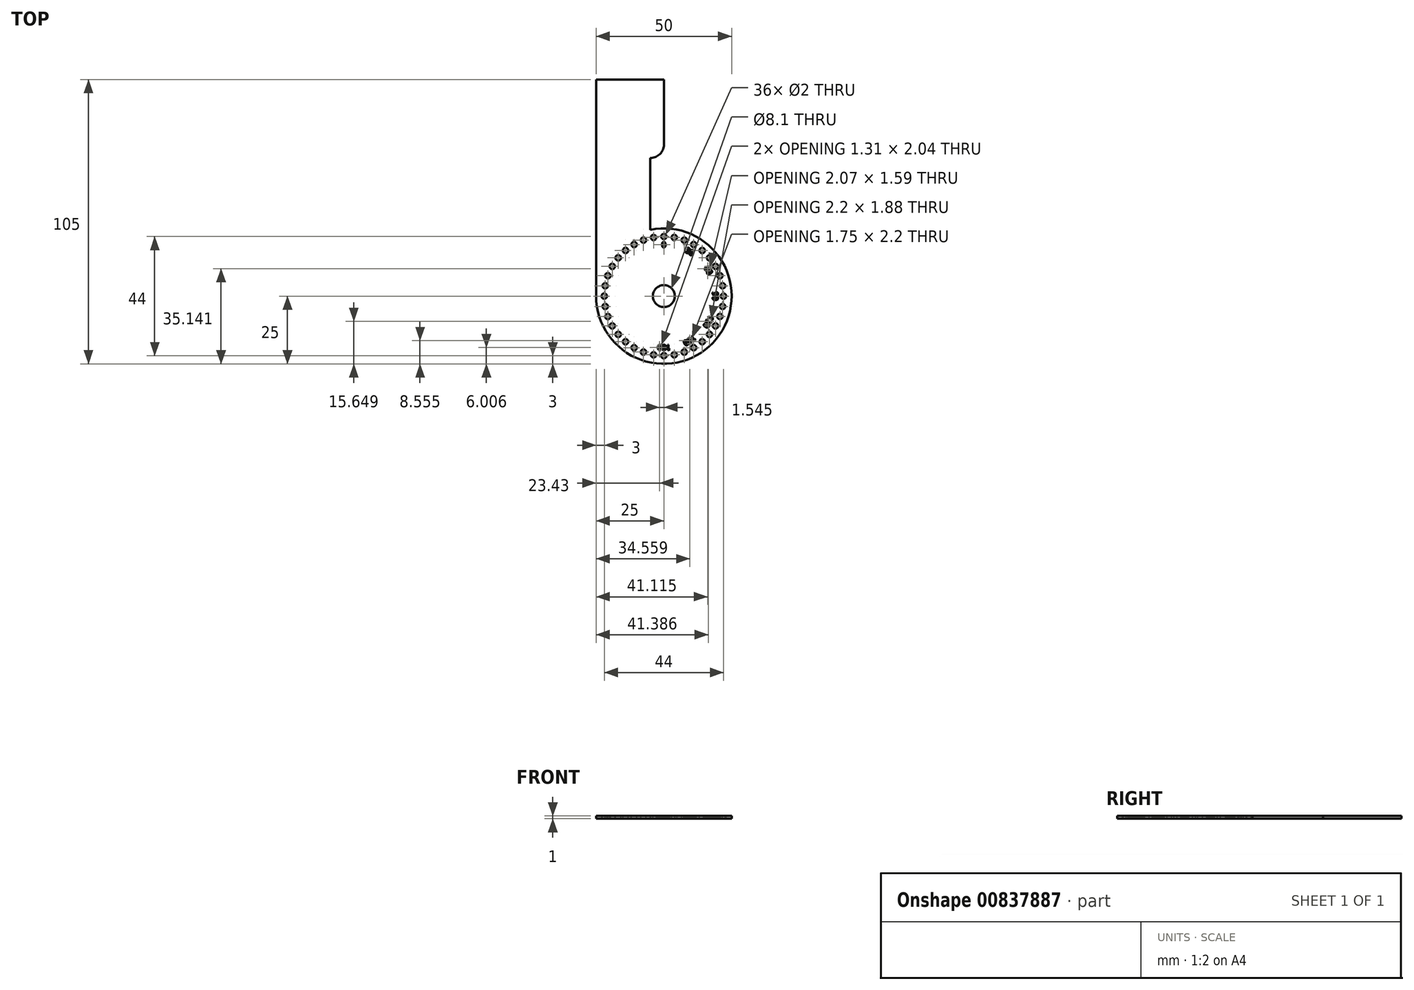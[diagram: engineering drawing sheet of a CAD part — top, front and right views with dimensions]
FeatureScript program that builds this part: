
annotation { "Feature Type Name" : "Feature", "Feature Type Description" : "" }
export const myFeature = defineFeature(function(context is Context, id is Id, definition is map)
    precondition{}
    {
        {
            var Q0;
            Q0=qCreatedBy(makeId("Top.planeOp"),FACE);
            var sketch = newSketch(context, id + "F0", { "sketchPlane" : qUnion([Q0])});
            skCircle(sketch, "E0", {"center": v(0, 0) * mm, "radius": 4.05 * mm});
            skCircle(sketch, "E1", {"center": v(0, 0) * mm, "radius": 25 * mm});
            skLineSegment(sketch, "E2.bottom", {"start": v(-25, 0) * mm, "end": v(25, 0) * mm});
            skLineSegment(sketch, "E2.top", {"start": v(-25, 80) * mm, "end": v(25, 80) * mm});
            skLineSegment(sketch, "E2.left", {"start": v(-25, 0) * mm, "end": v(-25, 80) * mm});
            skLineSegment(sketch, "E2.right", {"start": v(25, 0) * mm, "end": v(25, 80) * mm});
            skLineSegment(sketch, "E3.bottom", {"start": v(25, 65) * mm, "end": v(0, 65) * mm});
            skLineSegment(sketch, "E3.left", {"start": v(25, 65) * mm, "end": v(25, 35) * mm});
            skLineSegment(sketch, "E3.right", {"start": v(0, 65) * mm, "end": v(0, 60) * mm});
            skLineSegment(sketch, "E4", {"start": v(0, 60) * mm, "end": v(25, 35) * mm});
            skSolve(sketch);
        }
        {
            var Q0;
            {var subQ7=sQuery(id+"F0.wireOp",EDGE,"E2.top");Q0=makeQuery(id+"F0.imprint","IMPRINT",FACE,{"disambiguationData":[TD([[makeQuery(id+"F0.imprint","IMPRINT",EDGE,{"derivedFrom":subQ7}),-1.0]])]});}
            var Q1;
            {var subQ0=sQuery(id+"F0.wireOp",EDGE,"E2.bottom");var subQ1=sQuery(id+"F0.wireOp",EDGE,"E0");var subQ2=makeQuery(id+"F0.imprint","INTERSECT",VERTEX,{"disambiguationData":[OD(0.0)],"derivedFrom":[subQ1,subQ0]});Q1=makeQuery(id+"F0.imprint","IMPRINT",FACE,{"disambiguationData":[TD([[makeQuery(id+"F0.imprint","IMPRINT",EDGE,{"disambiguationData":[TD([[subQ2,1.0]])],"derivedFrom":subQ1}),-1.0]])]});}
            var Q2;
            {var subQ0=sQuery(id+"F0.wireOp",EDGE,"E2.bottom");var subQ1=sQuery(id+"F0.wireOp",EDGE,"E0");var subQ2=makeQuery(id+"F0.imprint","INTERSECT",VERTEX,{"disambiguationData":[OD(0.0)],"derivedFrom":[subQ1,subQ0]});Q2=makeQuery(id+"F0.imprint","IMPRINT",FACE,{"disambiguationData":[TD([[makeQuery(id+"F0.imprint","IMPRINT",EDGE,{"disambiguationData":[TD([[subQ2,-1.0]])],"derivedFrom":subQ1}),-1.0]])]});}
            var Q3;
            Q3=makeQuery(id+"F0.imprint","IMPRINT",FACE,{"disambiguationData":[TD([[makeQuery(id+"F0.imprint","IMPRINT",EDGE,{"derivedFrom":sQuery(id+"F0.wireOp",EDGE,"E3.bottom")}),1.0]])]});
            extrude(context, id + "F1", {"entities" : qUnion([Q0, Q1, Q2, Q3]), "oppositeDirection" : true, "depth" : 1 * mm, "offsetDistance" : 25 * mm});
        }
        {
            var Q0;
            Q0=makeQuery(id+"F1.opExtrude","CAP_FACE",FACE,{"disambiguationData":[OSD([sQuery(id+"F0.wireOp",EDGE,"E0"),sQuery(id+"F0.wireOp",EDGE,"E1"),sQuery(id+"F0.wireOp",EDGE,"E2.top"),sQuery(id+"F0.wireOp",EDGE,"E2.left"),sQuery(id+"F0.wireOp",EDGE,"E2.right"),sQuery(id+"F0.wireOp",EDGE,"E3.bottom"),sQuery(id+"F0.wireOp",EDGE,"E3.right"),sQuery(id+"F0.wireOp",EDGE,"E4")])],"isStart":true});
            var sketch = newSketch(context, id + "F2", { "sketchPlane" : qUnion([Q0])});
            skCircle(sketch, "E5", {"center": v(0, -22) * mm, "radius": 0.5 * mm});
            skPoint(sketch, "E5.centerSnap0", {"position": v(0, -25) * mm});
            skCircle(sketch, "E6.1.0", {"center": v(3.82, -21.67) * mm, "radius": 0.5 * mm});
            skCircle(sketch, "E6.2.0", {"center": v(7.52, -20.67) * mm, "radius": 0.5 * mm});
            skCircle(sketch, "E6.3.0", {"center": v(11, -19.05) * mm, "radius": 0.5 * mm});
            skCircle(sketch, "E6.4.0", {"center": v(14.14, -16.85) * mm, "radius": 0.5 * mm});
            skCircle(sketch, "E6.5.0", {"center": v(16.85, -14.14) * mm, "radius": 0.5 * mm});
            skCircle(sketch, "E6.6.0", {"center": v(19.05, -11) * mm, "radius": 0.5 * mm});
            skCircle(sketch, "E6.7.0", {"center": v(20.67, -7.52) * mm, "radius": 0.5 * mm});
            skCircle(sketch, "E6.8.0", {"center": v(21.67, -3.82) * mm, "radius": 0.5 * mm});
            skCircle(sketch, "E6.9.0", {"center": v(22, 0) * mm, "radius": 0.5 * mm});
            skCircle(sketch, "E6.10.0", {"center": v(21.67, 3.82) * mm, "radius": 0.5 * mm});
            skCircle(sketch, "E6.11.0", {"center": v(20.67, 7.52) * mm, "radius": 0.5 * mm});
            skCircle(sketch, "E6.12.0", {"center": v(19.05, 11) * mm, "radius": 0.5 * mm});
            skCircle(sketch, "E6.13.0", {"center": v(16.85, 14.14) * mm, "radius": 0.5 * mm});
            skCircle(sketch, "E6.14.0", {"center": v(14.14, 16.85) * mm, "radius": 0.5 * mm});
            skCircle(sketch, "E6.15.0", {"center": v(11, 19.05) * mm, "radius": 0.5 * mm});
            skCircle(sketch, "E6.16.0", {"center": v(7.52, 20.67) * mm, "radius": 0.5 * mm});
            skCircle(sketch, "E6.17.0", {"center": v(3.82, 21.67) * mm, "radius": 0.5 * mm});
            skCircle(sketch, "E6.18.0", {"center": v(0, 22) * mm, "radius": 0.5 * mm});
            skCircle(sketch, "E6.19.0", {"center": v(-3.82, 21.67) * mm, "radius": 0.5 * mm});
            skCircle(sketch, "E6.20.0", {"center": v(-7.52, 20.67) * mm, "radius": 0.5 * mm});
            skCircle(sketch, "E6.21.0", {"center": v(-11, 19.05) * mm, "radius": 0.5 * mm});
            skCircle(sketch, "E6.22.0", {"center": v(-14.14, 16.85) * mm, "radius": 0.5 * mm});
            skCircle(sketch, "E6.23.0", {"center": v(-16.85, 14.14) * mm, "radius": 0.5 * mm});
            skCircle(sketch, "E6.24.0", {"center": v(-19.05, 11) * mm, "radius": 0.5 * mm});
            skCircle(sketch, "E6.25.0", {"center": v(-20.67, 7.52) * mm, "radius": 0.5 * mm});
            skCircle(sketch, "E6.26.0", {"center": v(-21.67, 3.82) * mm, "radius": 0.5 * mm});
            skCircle(sketch, "E6.27.0", {"center": v(-22, 0) * mm, "radius": 0.5 * mm});
            skCircle(sketch, "E6.28.0", {"center": v(-21.67, -3.82) * mm, "radius": 0.5 * mm});
            skCircle(sketch, "E6.29.0", {"center": v(-20.67, -7.52) * mm, "radius": 0.5 * mm});
            skCircle(sketch, "E6.30.0", {"center": v(-19.05, -11) * mm, "radius": 0.5 * mm});
            skCircle(sketch, "E6.31.0", {"center": v(-16.85, -14.14) * mm, "radius": 0.5 * mm});
            skCircle(sketch, "E6.32.0", {"center": v(-14.14, -16.85) * mm, "radius": 0.5 * mm});
            skCircle(sketch, "E6.33.0", {"center": v(-11, -19.05) * mm, "radius": 0.5 * mm});
            skCircle(sketch, "E6.34.0", {"center": v(-7.52, -20.67) * mm, "radius": 0.5 * mm});
            skCircle(sketch, "E6.35.0", {"center": v(-3.82, -21.67) * mm, "radius": 0.5 * mm});
            skPoint(sketch, "E6.center", {"position": v(0, 0) * mm});
            skSolve(sketch);
        }
        {
            var Q0;
            Q0=sQuery(id+"F2.wireOp",VERTEX,"E5.center");
            var Q1;
            Q1=sQuery(id+"F2.wireOp",VERTEX,"E6.center");
            var Q2;
            Q2=sQuery(id+"F2.wireOp",VERTEX,"E6.61.0.center");
            var Q3;
            Q3=sQuery(id+"F2.wireOp",VERTEX,"E6.2.0.center");
            var Q4;
            Q4=sQuery(id+"F2.wireOp",VERTEX,"E6.49.0.center");
            var Q5;
            Q5=sQuery(id+"F2.wireOp",VERTEX,"E6.38.0.center");
            var Q6;
            Q6=sQuery(id+"F2.wireOp",VERTEX,"E6.1.0.center");
            var Q7;
            Q7=sQuery(id+"F2.wireOp",VERTEX,"E6.27.0.center");
            var Q8;
            Q8=sQuery(id+"F2.wireOp",VERTEX,"E6.8.0.center");
            var Q9;
            Q9=sQuery(id+"F2.wireOp",VERTEX,"E6.63.0.center");
            var Q10;
            Q10=sQuery(id+"F2.wireOp",VERTEX,"E6.28.0.center");
            var Q11;
            Q11=sQuery(id+"F2.wireOp",VERTEX,"E6.62.0.center");
            var Q12;
            Q12=sQuery(id+"F2.wireOp",VERTEX,"E6.66.0.center");
            var Q13;
            Q13=sQuery(id+"F2.wireOp",VERTEX,"E6.6.0.center");
            var Q14;
            Q14=sQuery(id+"F2.wireOp",VERTEX,"E6.58.0.center");
            var Q15;
            Q15=sQuery(id+"F2.wireOp",VERTEX,"E6.23.0.center");
            var Q16;
            Q16=sQuery(id+"F2.wireOp",VERTEX,"E6.26.0.center");
            var Q17;
            Q17=sQuery(id+"F2.wireOp",VERTEX,"E6.53.0.center");
            var Q18;
            Q18=sQuery(id+"F2.wireOp",VERTEX,"E6.13.0.center");
            var Q19;
            Q19=sQuery(id+"F2.wireOp",VERTEX,"E6.71.0.center");
            var Q20;
            Q20=sQuery(id+"F2.wireOp",VERTEX,"E6.34.0.center");
            var Q21;
            Q21=sQuery(id+"F2.wireOp",VERTEX,"E6.20.0.center");
            var Q22;
            Q22=sQuery(id+"F2.wireOp",VERTEX,"E6.59.0.center");
            var Q23;
            Q23=sQuery(id+"F2.wireOp",VERTEX,"E6.54.0.center");
            var Q24;
            Q24=sQuery(id+"F2.wireOp",VERTEX,"E6.22.0.center");
            var Q25;
            Q25=sQuery(id+"F2.wireOp",VERTEX,"E6.9.0.center");
            var Q26;
            Q26=sQuery(id+"F2.wireOp",VERTEX,"E6.32.0.center");
            var Q27;
            Q27=sQuery(id+"F2.wireOp",VERTEX,"E6.25.0.center");
            var Q28;
            Q28=sQuery(id+"F2.wireOp",VERTEX,"E6.64.0.center");
            var Q29;
            Q29=sQuery(id+"F2.wireOp",VERTEX,"E6.47.0.center");
            var Q30;
            Q30=sQuery(id+"F2.wireOp",VERTEX,"E6.31.0.center");
            var Q31;
            Q31=sQuery(id+"F2.wireOp",VERTEX,"E6.4.0.center");
            var Q32;
            Q32=sQuery(id+"F2.wireOp",VERTEX,"E6.15.0.center");
            var Q33;
            Q33=sQuery(id+"F2.wireOp",VERTEX,"E6.24.0.center");
            var Q34;
            Q34=sQuery(id+"F2.wireOp",VERTEX,"E6.29.0.center");
            var Q35;
            Q35=sQuery(id+"F2.wireOp",VERTEX,"E6.52.0.center");
            var Q36;
            Q36=sQuery(id+"F2.wireOp",VERTEX,"E6.7.0.center");
            var Q37;
            Q37=sQuery(id+"F2.wireOp",VERTEX,"E6.45.0.center");
            var Q38;
            Q38=sQuery(id+"F2.wireOp",VERTEX,"E6.42.0.center");
            var Q39;
            Q39=sQuery(id+"F2.wireOp",VERTEX,"E6.36.0.center");
            var Q40;
            Q40=sQuery(id+"F2.wireOp",VERTEX,"E6.17.0.center");
            var Q41;
            Q41=sQuery(id+"F2.wireOp",VERTEX,"E6.68.0.center");
            var Q42;
            Q42=sQuery(id+"F2.wireOp",VERTEX,"E6.18.0.center");
            var Q43;
            Q43=sQuery(id+"F2.wireOp",VERTEX,"E6.69.0.center");
            var Q44;
            Q44=sQuery(id+"F2.wireOp",VERTEX,"E6.56.0.center");
            var Q45;
            Q45=sQuery(id+"F2.wireOp",VERTEX,"E6.70.0.center");
            var Q46;
            Q46=sQuery(id+"F2.wireOp",VERTEX,"E6.48.0.center");
            var Q47;
            Q47=sQuery(id+"F2.wireOp",VERTEX,"E6.33.0.center");
            var Q48;
            Q48=sQuery(id+"F2.wireOp",VERTEX,"E6.10.0.center");
            var Q49;
            Q49=sQuery(id+"F2.wireOp",VERTEX,"E6.39.0.center");
            var Q50;
            Q50=sQuery(id+"F2.wireOp",VERTEX,"E6.55.0.center");
            var Q51;
            Q51=sQuery(id+"F2.wireOp",VERTEX,"E6.14.0.center");
            var Q52;
            Q52=sQuery(id+"F2.wireOp",VERTEX,"E6.21.0.center");
            var Q53;
            Q53=sQuery(id+"F2.wireOp",VERTEX,"E6.16.0.center");
            var Q54;
            Q54=sQuery(id+"F2.wireOp",VERTEX,"E6.65.0.center");
            var Q55;
            Q55=sQuery(id+"F2.wireOp",VERTEX,"E6.41.0.center");
            var Q56;
            Q56=sQuery(id+"F2.wireOp",VERTEX,"E6.3.0.center");
            var Q57;
            Q57=sQuery(id+"F2.wireOp",VERTEX,"E6.67.0.center");
            var Q58;
            Q58=sQuery(id+"F2.wireOp",VERTEX,"E6.19.0.center");
            var Q59;
            Q59=sQuery(id+"F2.wireOp",VERTEX,"E6.11.0.center");
            var Q60;
            Q60=sQuery(id+"F2.wireOp",VERTEX,"E6.57.0.center");
            var Q61;
            Q61=sQuery(id+"F2.wireOp",VERTEX,"E6.37.0.center");
            var Q62;
            Q62=sQuery(id+"F2.wireOp",VERTEX,"E6.51.0.center");
            var Q63;
            Q63=sQuery(id+"F2.wireOp",VERTEX,"E6.12.0.center");
            var Q64;
            Q64=sQuery(id+"F2.wireOp",VERTEX,"E6.50.0.center");
            var Q65;
            Q65=sQuery(id+"F2.wireOp",VERTEX,"E6.44.0.center");
            var Q66;
            Q66=sQuery(id+"F2.wireOp",VERTEX,"E6.35.0.center");
            var Q67;
            Q67=sQuery(id+"F2.wireOp",VERTEX,"E6.60.0.center");
            var Q68;
            Q68=sQuery(id+"F2.wireOp",VERTEX,"E6.5.0.center");
            var Q69;
            Q69=sQuery(id+"F2.wireOp",VERTEX,"E6.46.0.center");
            var Q70;
            Q70=sQuery(id+"F2.wireOp",VERTEX,"E6.43.0.center");
            var Q71;
            Q71=sQuery(id+"F2.wireOp",VERTEX,"E6.30.0.center");
            var Q72;
            Q72=sQuery(id+"F2.wireOp",VERTEX,"E6.40.0.center");
            var Q73;
            Q73=makeQuery(id+"F1.opExtrude","SWEPT_BODY",BODY,{"disambiguationData":[OSD([sQuery(id+"F0.wireOp",EDGE,"E0"),sQuery(id+"F0.wireOp",EDGE,"E1"),sQuery(id+"F0.wireOp",EDGE,"E2.top"),sQuery(id+"F0.wireOp",EDGE,"E2.left"),sQuery(id+"F0.wireOp",EDGE,"E2.right"),sQuery(id+"F0.wireOp",EDGE,"E3.bottom"),sQuery(id+"F0.wireOp",EDGE,"E3.right"),sQuery(id+"F0.wireOp",EDGE,"E4")])]});
            hole(context, id + "F3", {"style" : HoleStyle.SIMPLE, "endStyle" : HoleEndStyle.THROUGH, "holeDiameter" : 2 * mm, "majorDiameter" : 5 * mm, "isTappedThrough" : true, "tappedDepth" : 12 * mm, "tapClearance" : 3, "locations" : qUnion([Q0, Q1, Q2, Q3, Q4, Q5, Q6, Q7, Q8, Q9, Q10, Q11, Q12, Q13, Q14, Q15, Q16, Q17, Q18, Q19, Q20, Q21, Q22, Q23, Q24, Q25, Q26, Q27, Q28, Q29, Q30, Q31, Q32, Q33, Q34, Q35, Q36, Q37, Q38, Q39, Q40, Q41, Q42, Q43, Q44, Q45, Q46, Q47, Q48, Q49, Q50, Q51, Q52, Q53, Q54, Q55, Q56, Q57, Q58, Q59, Q60, Q61, Q62, Q63, Q64, Q65, Q66, Q67, Q68, Q69, Q70, Q71, Q72]), "scope" : qUnion([Q73])});
        }
        {
            var Q0;
            Q0=makeQuery(id+"F1.opExtrude","CAP_FACE",FACE,{"disambiguationData":[OSD([sQuery(id+"F0.wireOp",EDGE,"E0"),sQuery(id+"F0.wireOp",EDGE,"E1"),sQuery(id+"F0.wireOp",EDGE,"E2.top"),sQuery(id+"F0.wireOp",EDGE,"E2.left"),sQuery(id+"F0.wireOp",EDGE,"E2.right"),sQuery(id+"F0.wireOp",EDGE,"E3.bottom"),sQuery(id+"F0.wireOp",EDGE,"E3.right"),sQuery(id+"F0.wireOp",EDGE,"E4")])],"isStart":true});
            var sketch = newSketch(context, id + "F4", { "sketchPlane" : qUnion([Q0])});
            skText(sketch, "E7", { "text": "0", "fontName": "OpenSans-Regular.ttf"});
            const initialGuessF4  = {"E7": [-0.00082, 0.018, 1, 0, 0.002]};
            skSetInitialGuess(sketch, initialGuessF4);
            skSolve(sketch);
        }
        {
            var Q0;
            Q0 = qSketchRegion(id + "F4", true);
            extrude(context, id + "F5", {"entities" : qUnion([Q0]), "operationType" : NewBodyOperationType.REMOVE, "endBound" : BoundingType.UP_TO_NEXT, "oppositeDirection" : true, "depth" : 25 * mm, "offsetDistance" : 25 * mm});
        }
        {
            var Q0;
            {var subQ0=sQuery(id+"F0.wireOp",EDGE,"E2.left");var subQ1=sQuery(id+"F0.wireOp",EDGE,"E4");var subQ2=sQuery(id+"F0.wireOp",EDGE,"E0");var subQ3=sQuery(id+"F0.wireOp",EDGE,"E3.right");var subQ4=sQuery(id+"F0.wireOp",EDGE,"E2.right");var subQ5=sQuery(id+"F0.wireOp",EDGE,"E2.top");var subQ6=sQuery(id+"F0.wireOp",EDGE,"E1");var subQ7=sQuery(id+"F0.wireOp",EDGE,"E3.bottom");Q0=makeQuery(id+"F5.boolean.opBoolean","SPLIT",FACE,{"disambiguationData":[TD([makeQuery(id+"F1.opExtrude","SWEPT_FACE",FACE,{"disambiguationData":[OSD([subQ2])]})])],"derivedFrom":makeQuery(id+"F1.opExtrude","CAP_FACE",FACE,{"disambiguationData":[OSD([subQ2,subQ6,subQ5,subQ0,subQ4,subQ7,subQ3,subQ1])],"isStart":true})});}
            var sketch = newSketch(context, id + "F6", { "sketchPlane" : qUnion([Q0])});
            skText(sketch, "E8", { "text": "30\n", "fontName": "OpenSans-Regular.ttf"});
            skText(sketch, "E9", { "text": "90", "fontName": "OpenSans-Regular.ttf"});
            skLineSegment(sketch, "E10", {"start": v(0, 0) * mm, "end": v(9, 15.59) * mm, "construction": true});
            skLineSegment(sketch, "E11", {"start": v(0, 0) * mm, "end": v(4.05, 0) * mm, "construction": true});
            skText(sketch, "E12", { "text": "60", "fontName": "OpenSans-Regular.ttf"});
            skLineSegment(sketch, "E13", {"start": v(0, 0) * mm, "end": v(15.59, 9) * mm, "construction": true});
            skPoint(sketch, "E14.center", {"position": v(0, 0) * mm});
            const initialGuessF6  = {"E8": [0.0076, 0.0164, 0.86603, -0.5, 0.002], "E9": [0.018, 0.0016, 0, -1, 0.002], "E12": [0.01478, 0.0104, 0.5, -0.86603, 0.002]};
            skSetInitialGuess(sketch, initialGuessF6);
            skSolve(sketch);
        }
        {
            var Q0;
            Q0 = qSketchRegion(id + "F6", true);
            extrude(context, id + "F7", {"entities" : qUnion([Q0]), "operationType" : NewBodyOperationType.REMOVE, "oppositeDirection" : true, "depth" : 25 * mm, "offsetDistance" : 25 * mm});
        }
        {
            var Q0;
            {var subQ3=sQuery(id+"F0.wireOp",EDGE,"E4");var subQ5=sQuery(id+"F0.wireOp",EDGE,"E2.right");var subQ6=sQuery(id+"F0.wireOp",EDGE,"E2.top");var subQ8=sQuery(id+"F0.wireOp",EDGE,"E3.right");var subQ11=sQuery(id+"F0.wireOp",EDGE,"E2.left");var subQ13=sQuery(id+"F0.wireOp",EDGE,"E1");var subQ15=sQuery(id+"F0.wireOp",EDGE,"E0");var subQ16=makeQuery(id+"F1.opExtrude","SWEPT_FACE",FACE,{"disambiguationData":[OSD([subQ15])]});var subQ35=sQuery(id+"F0.wireOp",EDGE,"E3.bottom");Q0=makeQuery(id+"F7.boolean.opBoolean","SPLIT",FACE,{"disambiguationData":[TD([subQ16])],"derivedFrom":makeQuery(id+"F5.boolean.opBoolean","SPLIT",FACE,{"disambiguationData":[TD([subQ16])],"derivedFrom":makeQuery(id+"F1.opExtrude","CAP_FACE",FACE,{"disambiguationData":[OSD([subQ15,subQ13,subQ6,subQ11,subQ5,subQ35,subQ8,subQ3])],"isStart":true})})});}
            var sketch = newSketch(context, id + "F8", { "sketchPlane" : qUnion([Q0])});
            skLineSegment(sketch, "E15", {"start": v(0, 0) * mm, "end": v(4.05, 0) * mm, "construction": true});
            skLineSegment(sketch, "E16", {"start": v(0, 0) * mm, "end": v(15.59, -9) * mm, "construction": true});
            skLineSegment(sketch, "E17", {"start": v(0, 0) * mm, "end": v(9, -15.59) * mm, "construction": true});
            skLineSegment(sketch, "E18", {"start": v(0, 0) * mm, "end": v(0, -18) * mm, "construction": true});
            skText(sketch, "E19", { "text": "150", "fontName": "OpenSans-Regular.ttf"});
            skText(sketch, "E20", { "text": "180", "fontName": "OpenSans-Regular.ttf"});
            skText(sketch, "E21", { "text": "120", "fontName": "OpenSans-Regular.ttf"});
            skText(sketch, "E22", { "text": "120", "fontName": "OpenSans-Regular.ttf"});
            const initialGuessF8  = {"E19": [0.01108, -0.01439, -0.86603, -0.5, 0.002], "E20": [0.0024, -0.018, -1, 0, 0.002], "E21": [0.0168, -0.00692, -0.5, -0.86603, 0.002], "E22": [0.1751, 0.04347, 1, 0, 0.002]};
            skSetInitialGuess(sketch, initialGuessF8);
            skSolve(sketch);
        }
        {
            var Q0;
            Q0 = qSketchRegion(id + "F8", true);
            extrude(context, id + "F9", {"entities" : qUnion([Q0]), "operationType" : NewBodyOperationType.REMOVE, "oppositeDirection" : true, "depth" : 25 * mm, "offsetDistance" : 25 * mm});
        }
        {
            var Q0;
            {var subQ85=sQuery(id+"F0.wireOp",EDGE,"E0");var subQ86=makeQuery(id+"F1.opExtrude","SWEPT_FACE",FACE,{"disambiguationData":[OSD([subQ85])]});var subQ89=sQuery(id+"F0.wireOp",EDGE,"E2.left");var subQ120=sQuery(id+"F0.wireOp",EDGE,"E1");var subQ124=sQuery(id+"F0.wireOp",EDGE,"E2.top");var subQ127=sQuery(id+"F0.wireOp",EDGE,"E3.left");var subQ128=sQuery(id+"F0.wireOp",EDGE,"E2.right");Q0=makeQuery(id+"F9.boolean.opBoolean","SPLIT",FACE,{"disambiguationData":[TD([subQ86])],"derivedFrom":makeQuery(id+"F7.boolean.opBoolean","SPLIT",FACE,{"disambiguationData":[TD([subQ86])],"derivedFrom":makeQuery(id+"F5.boolean.opBoolean","SPLIT",FACE,{"disambiguationData":[TD([subQ86])],"derivedFrom":makeQuery(id+"F1.opExtrude","CAP_FACE",FACE,{"disambiguationData":[OSD([subQ85,subQ120,subQ124,subQ89,subQ128,subQ127])],"isStart":true})})})});}
            var sketch = newSketch(context, id + "F10", { "sketchPlane" : qUnion([Q0])});
            skCircle(sketch, "E23", {"center": v(0, 0) * mm, "radius": 25 * mm});
            skLineSegment(sketch, "E24", {"start": v(-5, 24.5) * mm, "end": v(-5, 51) * mm});
            skArc(sketch, "E25", {"start": v(-5, 51) * mm, "mid": v(-1.46, 52.46) * mm, "end": v(0, 56) * mm});
            skLineSegment(sketch, "E26", {"start": v(0, 80) * mm, "end": v(0, 56) * mm});
            skSolve(sketch);
        }
        {
            var Q0;
            {var subQ0=sQuery(id+"F10.wireOp",EDGE,"E24");Q0=makeQuery(id+"F10.imprint","IMPRINT",FACE,{"disambiguationData":[TD([[makeQuery(id+"F10.imprint","IMPRINT",EDGE,{"derivedFrom":subQ0}),-1.0]])]});}
            extrude(context, id + "F11", {"entities" : qUnion([Q0]), "operationType" : NewBodyOperationType.REMOVE, "endBound" : BoundingType.UP_TO_NEXT, "oppositeDirection" : true, "depth" : 25 * mm, "offsetDistance" : 25 * mm});
        }
    });
